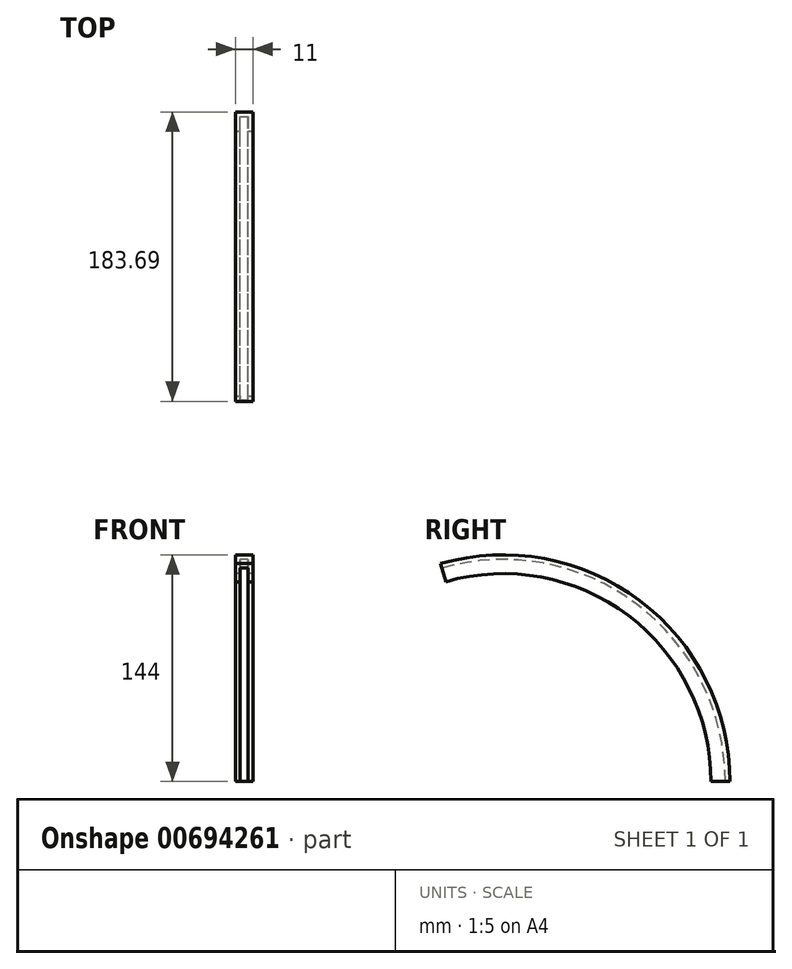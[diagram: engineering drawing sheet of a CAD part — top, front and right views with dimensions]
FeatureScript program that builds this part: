
annotation { "Feature Type Name" : "Feature", "Feature Type Description" : "" }
export const myFeature = defineFeature(function(context is Context, id is Id, definition is map)
    precondition{}
    {
        {
            var Q0;
            Q0=qCreatedBy(makeId("Top.planeOp"),FACE);
            var sketch = newSketch(context, id + "F0", { "sketchPlane" : qUnion([Q0])});
            skLineSegment(sketch, "E0.bottom", {"start": v(-5.63, 12) * mm, "end": v(5.37, 12) * mm});
            skLineSegment(sketch, "E0.top", {"start": v(-5.63, 0) * mm, "end": v(-2.63, 0) * mm});
            skLineSegment(sketch, "E0.left", {"start": v(-5.63, 12) * mm, "end": v(-5.63, 0) * mm});
            skLineSegment(sketch, "E0.right", {"start": v(5.37, 12) * mm, "end": v(5.37, 0) * mm});
            skLineSegment(sketch, "E1", {"start": v(-2.63, 0) * mm, "end": v(-2.63, 9) * mm});
            skLineSegment(sketch, "E2", {"start": v(-2.63, 9) * mm, "end": v(2.37, 9) * mm});
            skLineSegment(sketch, "E3", {"start": v(2.37, 9) * mm, "end": v(2.37, 0) * mm});
            skLineSegment(sketch, "E4.trimOffspring", {"start": v(2.37, 0) * mm, "end": v(5.37, 0) * mm});
            skLineSegment(sketch, "E5", {"start": v(0, 0) * mm, "end": v(0, -132) * mm});
            skSolve(sketch);
        }
        {
            var Q0;
            Q0=qCreatedBy(makeId("Right.planeOp"),FACE);
            var sketch = newSketch(context, id + "F1", { "sketchPlane" : qUnion([Q0])});
            skLineSegment(sketch, "E6", {"start": v(0, 0) * mm, "end": v(-132, 0) * mm});
            skCircle(sketch, "E7", {"center": v(-132, 0) * mm, "radius": 144 * mm});
            skSolve(sketch);
        }
        {
            var Q0;
            Q0=makeQuery(id+"F0.imprint","IMPRINT",FACE,{"disambiguationData":[TD([[makeQuery(id+"F0.imprint","IMPRINT",EDGE,{"derivedFrom":sQuery(id+"F0.wireOp",EDGE,"E0.bottom")}),-1.0]])]});
            var Q1;
            Q1=sQuery(id+"F1.wireOp",EDGE,"E7");
            revolve(context, id + "F2", {"entities" : qUnion([Q0]), "axis" : qUnion([Q1]), "revolveType" : RevolveType.ONE_DIRECTION, "angle" : 106 * degree});
        }
    });
